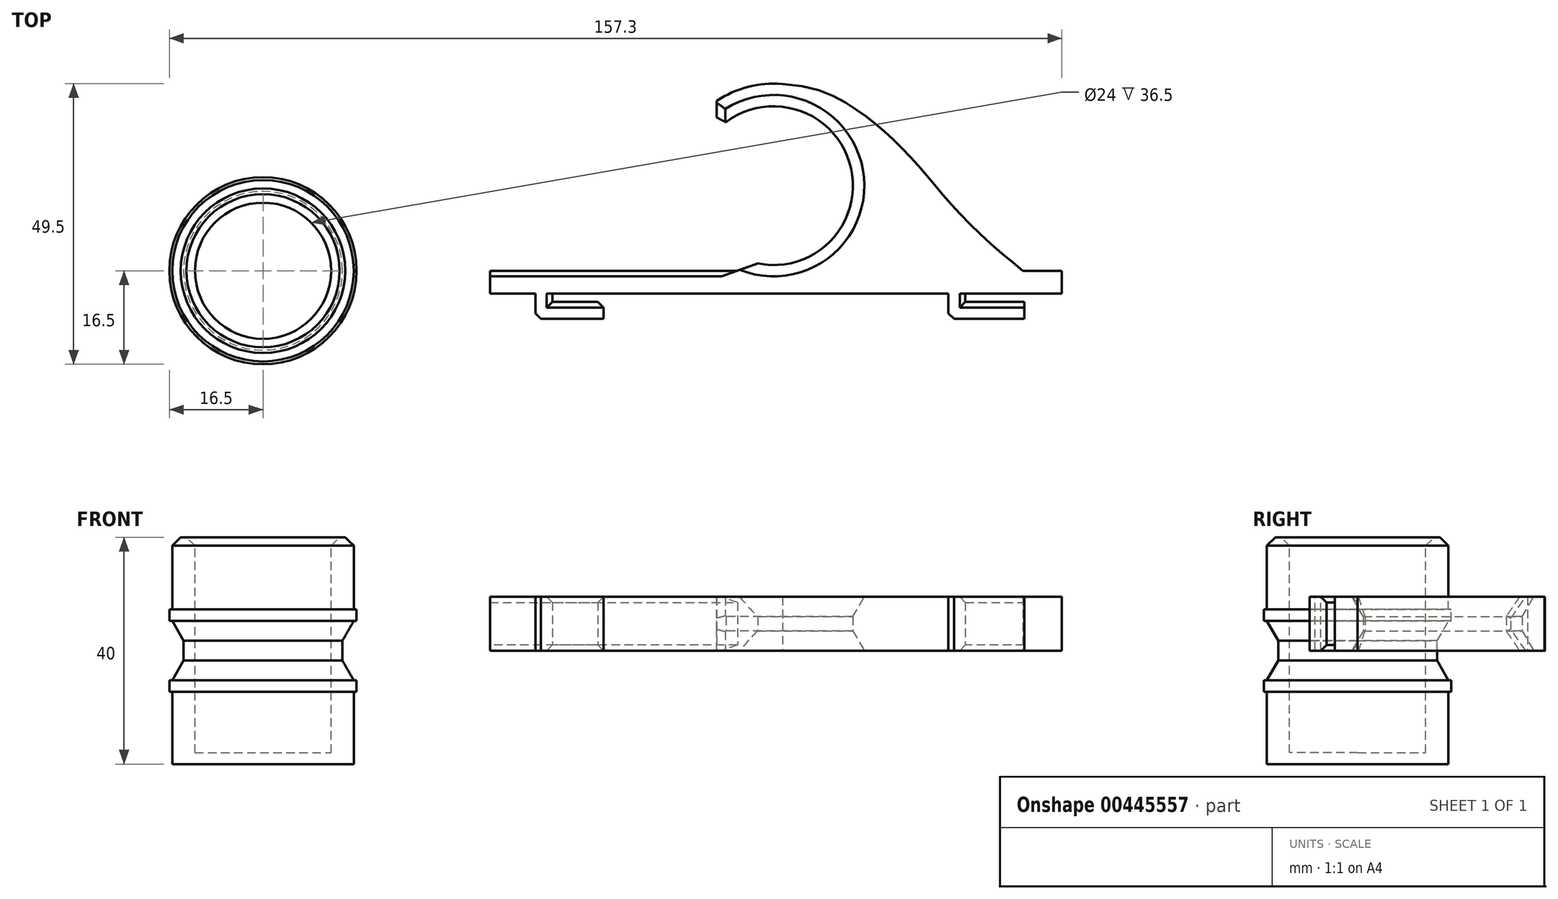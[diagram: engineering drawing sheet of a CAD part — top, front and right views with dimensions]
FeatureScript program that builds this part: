
annotation { "Feature Type Name" : "Feature", "Feature Type Description" : "" }
export const myFeature = defineFeature(function(context is Context, id is Id, definition is map)
    precondition{}
    {
        {
            var Q0;
            Q0=qCreatedBy(makeId("Top.planeOp"),FACE);
            var sketch = newSketch(context, id + "F0", { "sketchPlane" : qUnion([Q0])});
            skLineSegment(sketch, "E0", {"start": v(0, 0) * mm, "end": v(60.8, 0) * mm});
            skLineSegment(sketch, "E1", {"start": v(0, 0) * mm, "end": v(-12, 0) * mm});
            skLineSegment(sketch, "E2", {"start": v(-12, -4) * mm, "end": v(-12, -8.5) * mm});
            skLineSegment(sketch, "E3", {"start": v(-12, -8.5) * mm, "end": v(0, -8.5) * mm});
            skLineSegment(sketch, "E4", {"start": v(0, -8.5) * mm, "end": v(0, -5.5) * mm});
            skLineSegment(sketch, "E5", {"start": v(0, -5.5) * mm, "end": v(-9, -5.5) * mm});
            skLineSegment(sketch, "E6", {"start": v(-9, -5.5) * mm, "end": v(-9, -4) * mm});
            skLineSegment(sketch, "E7", {"start": v(-9, -4) * mm, "end": v(0, -4) * mm});
            skLineSegment(sketch, "E8", {"start": v(60.8, -4) * mm, "end": v(60.8, -8.5) * mm});
            skLineSegment(sketch, "E9", {"start": v(60.8, -8.5) * mm, "end": v(74.2, -8.5) * mm});
            skLineSegment(sketch, "E10", {"start": v(74.2, -8.5) * mm, "end": v(74.2, -5.5) * mm});
            skLineSegment(sketch, "E11", {"start": v(74.2, -5.5) * mm, "end": v(63.8, -5.5) * mm});
            skLineSegment(sketch, "E12", {"start": v(63.8, -5.5) * mm, "end": v(63.8, -4) * mm});
            skLineSegment(sketch, "E13", {"start": v(63.8, -4) * mm, "end": v(74.2, -4) * mm});
            skLineSegment(sketch, "E14", {"start": v(72.8, 0) * mm, "end": v(60.8, 0) * mm});
            skLineSegment(sketch, "E15", {"start": v(-12, 0) * mm, "end": v(-20, 0) * mm});
            skLineSegment(sketch, "E16", {"start": v(80.8, 0) * mm, "end": v(72.8, 0) * mm});
            skLineSegment(sketch, "E17", {"start": v(-20, 0) * mm, "end": v(-20, -4) * mm});
            skLineSegment(sketch, "E18", {"start": v(-20, -4) * mm, "end": v(-12, -4) * mm});
            skLineSegment(sketch, "E19", {"start": v(80.8, 0) * mm, "end": v(80.8, -4) * mm});
            skLineSegment(sketch, "E20", {"start": v(80.8, -4) * mm, "end": v(74.2, -4) * mm});
            skLineSegment(sketch, "E21", {"start": v(0, -4) * mm, "end": v(60.8, -4) * mm});
            skSolve(sketch);
        }
        {
            var Q0;
            Q0 = qSketchRegion(id + "F0", true);
            extrude(context, id + "F1", {"entities" : qUnion([Q0]), "depth" : 9.5 * mm});
        }
        {
            var Q0;
            Q0=makeQuery(id+"F1.opExtrude","SWEPT_EDGE",EDGE,{"disambiguationData":[OSD([sQuery(id+"F0.wireOp",EDGE,"E2"),sQuery(id+"F0.wireOp",EDGE,"E3")])]});
            var Q1;
            Q1=makeQuery(id+"F1.opExtrude","SWEPT_EDGE",EDGE,{"disambiguationData":[OSD([sQuery(id+"F0.wireOp",EDGE,"E8"),sQuery(id+"F0.wireOp",EDGE,"E9")])]});
            var Q2;
            Q2=makeQuery(id+"F1.opExtrude","SWEPT_EDGE",EDGE,{"disambiguationData":[OSD([sQuery(id+"F0.wireOp",EDGE,"E4"),sQuery(id+"F0.wireOp",EDGE,"E5")])]});
            var Q3;
            Q3=makeQuery(id+"F1.opExtrude","CAP_EDGE",EDGE,{"disambiguationData":[OSD([sQuery(id+"F0.wireOp",EDGE,"E11")])],"isStart":true});
            var Q4;
            Q4=makeQuery(id+"F1.opExtrude","CAP_EDGE",EDGE,{"disambiguationData":[OSD([sQuery(id+"F0.wireOp",EDGE,"E5")])],"isStart":true});
            var Q5;
            Q5=makeQuery(id+"F1.opExtrude","CAP_EDGE",EDGE,{"disambiguationData":[OSD([sQuery(id+"F0.wireOp",EDGE,"E6")])],"isStart":true});
            var Q6;
            Q6=makeQuery(id+"F1.opExtrude","CAP_EDGE",EDGE,{"disambiguationData":[OSD([sQuery(id+"F0.wireOp",EDGE,"E12")])],"isStart":true});
            var Q7;
            Q7=makeQuery(id+"F1.opExtrude","CAP_EDGE",EDGE,{"disambiguationData":[OSD([sQuery(id+"F0.wireOp",EDGE,"E11")])],"isStart":false});
            var Q8;
            Q8=makeQuery(id+"F1.opExtrude","CAP_EDGE",EDGE,{"disambiguationData":[OSD([sQuery(id+"F0.wireOp",EDGE,"E12")])],"isStart":false});
            var Q9;
            Q9=makeQuery(id+"F1.opExtrude","CAP_EDGE",EDGE,{"disambiguationData":[OSD([sQuery(id+"F0.wireOp",EDGE,"E5")])],"isStart":false});
            var Q10;
            Q10=makeQuery(id+"F1.opExtrude","CAP_EDGE",EDGE,{"disambiguationData":[OSD([sQuery(id+"F0.wireOp",EDGE,"E6")])],"isStart":false});
            chamfer(context, id + "F2", {"entities" : qUnion([Q0, Q1, Q2, Q3, Q4, Q5, Q6, Q7, Q8, Q9, Q10]), "width" : 1 * mm, "tangentPropagation" : true});
        }
        {
            var Q0;
            Q0=qCreatedBy(makeId("Top.planeOp"),FACE);
            var sketch = newSketch(context, id + "F3", { "sketchPlane" : qUnion([Q0])});
            skArc(sketch, "E22", {"start": v(27.2, 1.28) * mm, "mid": v(43.39, 19.1) * mm, "end": v(20, 24.8) * mm});
            skArc(sketch, "E23", {"start": v(31.56, 32.93) * mm, "mid": v(25.53, 32.44) * mm, "end": v(20, 29.97) * mm});
            skLineSegment(sketch, "E24", {"start": v(20, 24.8) * mm, "end": v(20, 29.97) * mm});
            skLineSegment(sketch, "E25", {"start": v(27.2, 1.28) * mm, "end": v(27.2, 0) * mm});
            skLineSegment(sketch, "E26", {"start": v(27.2, 0) * mm, "end": v(73.96, 0) * mm});
            skLineSegment(sketch, "E27", {"start": v(27.2, 1.28) * mm, "end": v(23.63, 0) * mm});
            skLineSegment(sketch, "E28", {"start": v(23.63, 0) * mm, "end": v(27.2, 0) * mm});
            skFitSpline(sketch, "E29", {"points": [v(31.56, 32.93) * mm, v(43.72, 29) * mm, v(49.62, 24.5) * mm, v(54.75, 19.36) * mm, v(59.98, 13.26) * mm, v(66.26, 6.61) * mm, v(73.96, 0) * mm], "startDerivative": vector(86.62, -3.3) * mm, "endDerivative": vector(37.5, -30.04) * mm});
            skSolve(sketch);
        }
        {
            var Q0;
            Q0 = qSketchRegion(id + "F3", true);
            extrude(context, id + "F4", {"entities" : qUnion([Q0]), "operationType" : NewBodyOperationType.ADD, "depth" : 9.5 * mm});
        }
        {
            var Q0;
            Q0=makeQuery(id+"F4.opExtrude","CAP_EDGE",EDGE,{"disambiguationData":[OSD([sQuery(id+"F3.wireOp",EDGE,"E22")])],"isStart":false});
            var Q1;
            Q1=makeQuery(id+"F4.opExtrude","CAP_EDGE",EDGE,{"disambiguationData":[OSD([sQuery(id+"F3.wireOp",EDGE,"E22")])],"isStart":true});
            chamfer(context, id + "F5", {"entities" : qUnion([Q0, Q1]), "chamferType" : ChamferType.TWO_OFFSETS, "width1" : 3.5 * mm, "oppositeDirection" : false, "width2" : 2 * mm, "tangentPropagation" : true});
        }
        {
            var Q0;
            {var subQ0=sQuery(id+"F0.wireOp",EDGE,"E17");var subQ1=sQuery(id+"F0.wireOp",EDGE,"E16");var subQ2=sQuery(id+"F0.wireOp",EDGE,"E15");var subQ3=sQuery(id+"F0.wireOp",EDGE,"E14");var subQ4=sQuery(id+"F0.wireOp",EDGE,"E1");var subQ5=sQuery(id+"F0.wireOp",EDGE,"E0");Q0=makeQuery(id+"F4.boolean.opBoolean","SPLIT",EDGE,{"disambiguationData":[TD([makeQuery(id+"F1.opExtrude","SWEPT_FACE",FACE,{"disambiguationData":[OSD([subQ0])]})])],"derivedFrom":makeQuery(id+"F1.opExtrude","CAP_EDGE",EDGE,{"disambiguationData":[OSD([subQ5,subQ4,subQ3,subQ2,subQ1])],"isStart":false})});}
            var Q1;
            {var subQ0=sQuery(id+"F0.wireOp",EDGE,"E16");var subQ1=sQuery(id+"F0.wireOp",EDGE,"E15");var subQ2=sQuery(id+"F0.wireOp",EDGE,"E14");var subQ3=sQuery(id+"F0.wireOp",EDGE,"E1");var subQ4=sQuery(id+"F0.wireOp",EDGE,"E0");var subQ6=sQuery(id+"F0.wireOp",EDGE,"E17");Q1=makeQuery(id+"F4.boolean.opBoolean","SPLIT",EDGE,{"disambiguationData":[TD([makeQuery(id+"F1.opExtrude","SWEPT_FACE",FACE,{"disambiguationData":[OSD([subQ6])]})])],"derivedFrom":makeQuery(id+"F1.opExtrude","CAP_EDGE",EDGE,{"disambiguationData":[OSD([subQ4,subQ3,subQ2,subQ1,subQ0])],"isStart":true})});}
            var Q2;
            Q2=makeQuery(id+"F4.opExtrude","CAP_EDGE",EDGE,{"disambiguationData":[OSD([sQuery(id+"F3.wireOp",EDGE,"ECYqVk7i-5rVQ-H3yP-Ue2O-Aet6nYUCdmsS")])],"isStart":true});
            var Q3;
            Q3=makeQuery(id+"F4.opExtrude","SWEPT_EDGE",EDGE,{"disambiguationData":[OSD([sQuery(id+"F3.wireOp",EDGE,"E22"),sQuery(id+"F3.wireOp",EDGE,"E24")])]});
            var Q4;
            Q4=makeQuery(id+"F5.opChamfer","BLEND_EDGE",EDGE,{"blendedFrom":[makeQuery(id+"F4.opExtrude","CAP_EDGE",EDGE,{"disambiguationData":[OSD([sQuery(id+"F3.wireOp",EDGE,"E22")])],"isStart":false}),makeQuery(id+"F4.opExtrude","SWEPT_FACE",FACE,{"disambiguationData":[OSD([sQuery(id+"F3.wireOp",EDGE,"E24")])]})],"blendedInto":[makeQuery(id+"F4.opExtrude","SWEPT_FACE",FACE,{"disambiguationData":[OSD([sQuery(id+"F3.wireOp",EDGE,"E24")])]})]});
            var Q5;
            Q5=makeQuery(id+"F5.opChamfer","BLEND_EDGE",EDGE,{"blendedFrom":[makeQuery(id+"F4.opExtrude","CAP_EDGE",EDGE,{"disambiguationData":[OSD([sQuery(id+"F3.wireOp",EDGE,"E22")])],"isStart":true}),makeQuery(id+"F4.opExtrude","SWEPT_FACE",FACE,{"disambiguationData":[OSD([sQuery(id+"F3.wireOp",EDGE,"E24")])]})],"blendedInto":[makeQuery(id+"F4.opExtrude","SWEPT_FACE",FACE,{"disambiguationData":[OSD([sQuery(id+"F3.wireOp",EDGE,"E24")])]})]});
            chamfer(context, id + "F6", {"entities" : qUnion([Q0, Q1, Q2, Q3, Q4, Q5]), "width" : 1 * mm, "tangentPropagation" : true});
        }
        {
            var Q0;
            Q0=qCreatedBy(makeId("Front.planeOp"),FACE);
            var sketch = newSketch(context, id + "F7", { "sketchPlane" : qUnion([Q0])});
            skLineSegment(sketch, "E30", {"start": v(0, 0) * mm, "end": v(-60, 0) * mm});
            skLineSegment(sketch, "E31", {"start": v(-60, 0) * mm, "end": v(-60, -12.67) * mm});
            skLineSegment(sketch, "E32", {"start": v(-60, 0) * mm, "end": v(-72, 0) * mm});
            skLineSegment(sketch, "E33", {"start": v(-72, 0) * mm, "end": v(-76, 0) * mm});
            skLineSegment(sketch, "E34", {"start": v(-72, 0) * mm, "end": v(-72, 20) * mm});
            skLineSegment(sketch, "E35", {"start": v(-72, 20) * mm, "end": v(-76, 20) * mm});
            skLineSegment(sketch, "E36", {"start": v(-76, 20) * mm, "end": v(-76, 5.25) * mm});
            skLineSegment(sketch, "E37", {"start": v(-76, 5.25) * mm, "end": v(-74, 1.75) * mm});
            skLineSegment(sketch, "E38", {"start": v(-74, 1.75) * mm, "end": v(-74, 0) * mm});
            skLineSegment(sketch, "E39.MirrorCS", {"start": v(-74, -1.75) * mm, "end": v(-74, 0) * mm});
            skLineSegment(sketch, "E40.MirrorCS", {"start": v(-76, -5.25) * mm, "end": v(-74, -1.75) * mm});
            skLineSegment(sketch, "E41.MirrorCS", {"start": v(-76, -20) * mm, "end": v(-76, -5.25) * mm});
            skLineSegment(sketch, "E42.MirrorCS", {"start": v(-72, -20) * mm, "end": v(-76, -20) * mm});
            skLineSegment(sketch, "E43.MirrorCS", {"start": v(-72, 0) * mm, "end": v(-72, -20) * mm});
            skLineSegment(sketch, "E44", {"start": v(-76, 5.25) * mm, "end": v(-76.5, 5.25) * mm});
            skLineSegment(sketch, "E45", {"start": v(-76.5, 5.25) * mm, "end": v(-76.5, 7.25) * mm});
            skLineSegment(sketch, "E46", {"start": v(-76.5, 7.25) * mm, "end": v(-76, 7.25) * mm});
            skLineSegment(sketch, "E47.MirrorCS", {"start": v(-76.5, -7.25) * mm, "end": v(-76, -7.25) * mm});
            skLineSegment(sketch, "E48.MirrorCS", {"start": v(-76.5, -5.25) * mm, "end": v(-76.5, -7.25) * mm});
            skLineSegment(sketch, "E49.MirrorCS", {"start": v(-76, -5.25) * mm, "end": v(-76.5, -5.25) * mm});
            skSolve(sketch);
        }
        {
            var Q0;
            Q0 = qSketchRegion(id + "F7", true);
            var Q1;
            Q1=sQuery(id+"F7.wireOp",EDGE,"E31");
            revolve(context, id + "F8", {"entities" : qUnion([Q0]), "axis" : qUnion([Q1]), "revolveType" : RevolveType.FULL});
        }
        {
            var Q0;
            Q0=makeQuery(id+"F8.opRevolve","SWEPT_FACE",FACE,{"disambiguationData":[OSD([sQuery(id+"F7.wireOp",EDGE,"E35")])]});
            chamfer(context, id + "F9", {"entities" : qUnion([Q0]), "width" : 1.5 * mm, "tangentPropagation" : true});
        }
        {
            var Q0;
            Q0=makeQuery(id+"F8.opRevolve","SWEPT_FACE",FACE,{"disambiguationData":[OSD([sQuery(id+"F7.wireOp",EDGE,"E42.MirrorCS")])]});
            var sketch = newSketch(context, id + "F10", { "sketchPlane" : qUnion([Q0])});
            skCircle(sketch, "E50", {"center": v(-60, 0) * mm, "radius": 16 * mm});
            skSolve(sketch);
        }
        {
            var Q0;
            Q0 = qSketchRegion(id + "F10", true);
            extrude(context, id + "F11", {"entities" : qUnion([Q0]), "operationType" : NewBodyOperationType.ADD, "oppositeDirection" : true, "depth" : 2 * mm});
        }
    });
